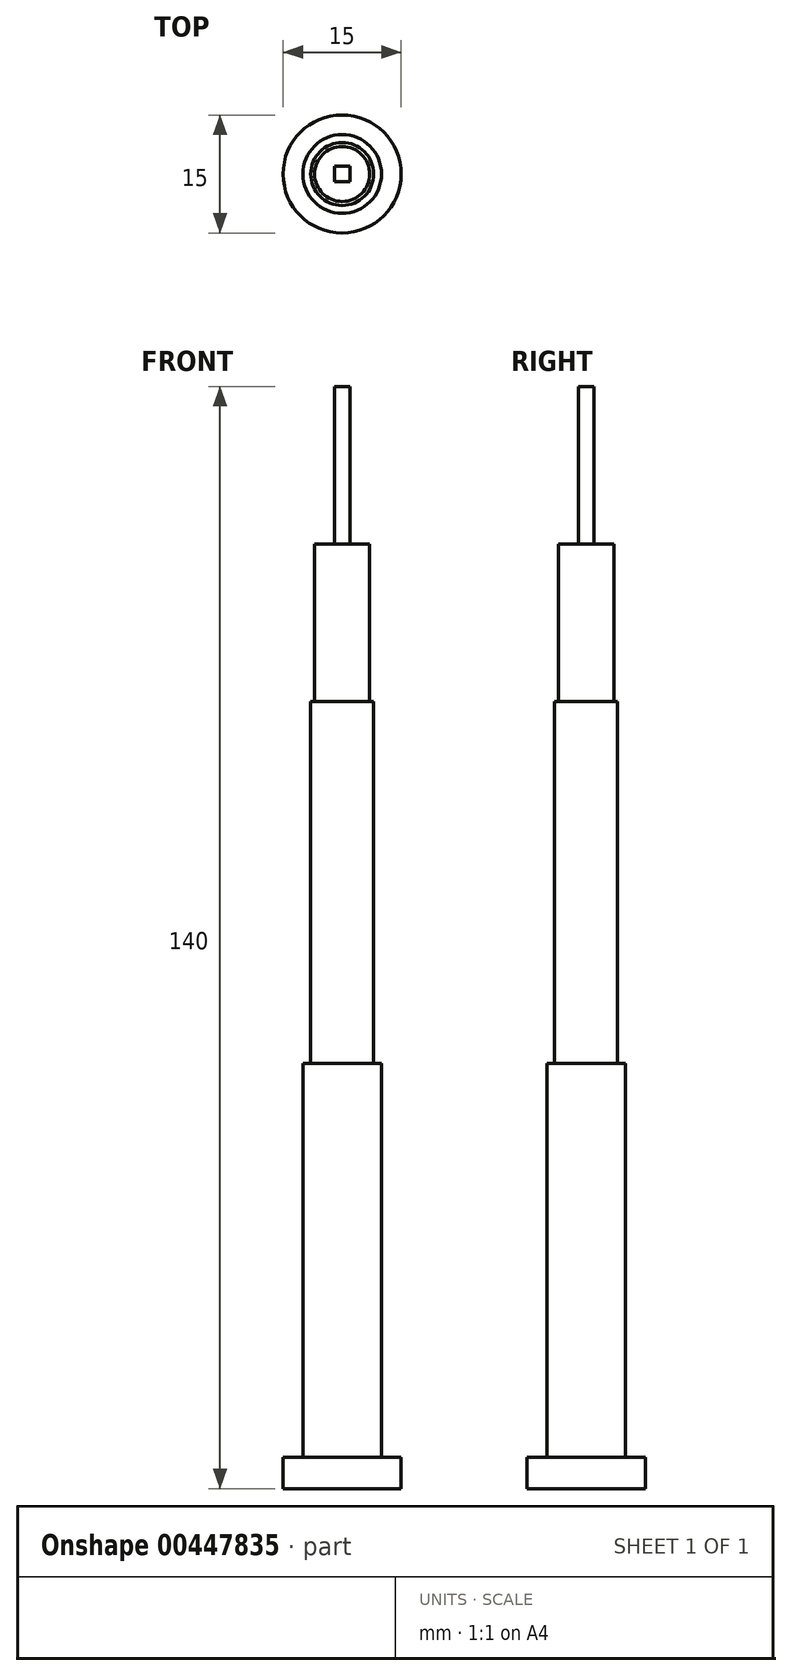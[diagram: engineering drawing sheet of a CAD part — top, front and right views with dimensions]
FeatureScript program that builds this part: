
annotation { "Feature Type Name" : "Feature", "Feature Type Description" : "" }
export const myFeature = defineFeature(function(context is Context, id is Id, definition is map)
    precondition{}
    {
        {
            var Q0;
            Q0=qCreatedBy(makeId("Top.planeOp"),FACE);
            var sketch = newSketch(context, id + "F0", { "sketchPlane" : qUnion([Q0])});
            skCircle(sketch, "E0", {"center": v(0, 0) * mm, "radius": 7.5 * mm});
            skSolve(sketch);
        }
        {
            var Q0;
            Q0=qSketchRegion(id+"F0",true);
            extrude(context, id + "F1", {"entities" : qUnion([Q0]), "depth" : 4 * mm});
        }
        {
            var Q0;
            Q0=qCreatedBy(makeId("Top.planeOp"),FACE);
            var sketch = newSketch(context, id + "F2", { "sketchPlane" : qUnion([Q0])});
            skCircle(sketch, "E1", {"center": v(0, 0) * mm, "radius": 5 * mm});
            skSolve(sketch);
        }
        {
            var Q0;
            Q0=qSketchRegion(id+"F2",true);
            extrude(context, id + "F3", {"entities" : qUnion([Q0]), "operationType" : NewBodyOperationType.ADD, "depth" : 54 * mm});
        }
        {
            var Q0;
            Q0=makeQuery(id+"F3.opExtrude","CAP_FACE",FACE,{"disambiguationData":[OSD([sQuery(id+"F2.wireOp",EDGE,"E1")])],"isStart":false});
            var sketch = newSketch(context, id + "F4", { "sketchPlane" : qUnion([Q0])});
            skCircle(sketch, "E2", {"center": v(0, 0) * mm, "radius": 4 * mm});
            skSolve(sketch);
        }
        {
            var Q0;
            Q0=qSketchRegion(id+"F4",true);
            extrude(context, id + "F5", {"entities" : qUnion([Q0]), "operationType" : NewBodyOperationType.ADD, "depth" : 46 * mm});
        }
        {
            var Q0;
            Q0=makeQuery(id+"F5.opExtrude","CAP_FACE",FACE,{"disambiguationData":[OSD([sQuery(id+"F4.wireOp",EDGE,"E2")])],"isStart":false});
            var sketch = newSketch(context, id + "F6", { "sketchPlane" : qUnion([Q0])});
            skCircle(sketch, "E3", {"center": v(0, 0) * mm, "radius": 3.5 * mm});
            skSolve(sketch);
        }
        {
            var Q0;
            Q0=qSketchRegion(id+"F6",true);
            extrude(context, id + "F7", {"entities" : qUnion([Q0]), "operationType" : NewBodyOperationType.ADD, "depth" : 20 * mm});
        }
        {
            var Q0;
            Q0=makeQuery(id+"F7.opExtrude","CAP_FACE",FACE,{"disambiguationData":[OSD([sQuery(id+"F6.wireOp",EDGE,"E3")])],"isStart":false});
            var sketch = newSketch(context, id + "F8", { "sketchPlane" : qUnion([Q0])});
            skLineSegment(sketch, "E4.bottom", {"start": v(-1, 1) * mm, "end": v(1, 1) * mm});
            skLineSegment(sketch, "E4.top", {"start": v(-1, -1) * mm, "end": v(1, -1) * mm});
            skLineSegment(sketch, "E4.left", {"start": v(-1, 1) * mm, "end": v(-1, -1) * mm});
            skLineSegment(sketch, "E4.right", {"start": v(1, 1) * mm, "end": v(1, -1) * mm});
            skSolve(sketch);
        }
        {
            var Q0;
            Q0=qSketchRegion(id+"F8",true);
            extrude(context, id + "F9", {"entities" : qUnion([Q0]), "operationType" : NewBodyOperationType.ADD, "depth" : 20 * mm});
        }
    });
